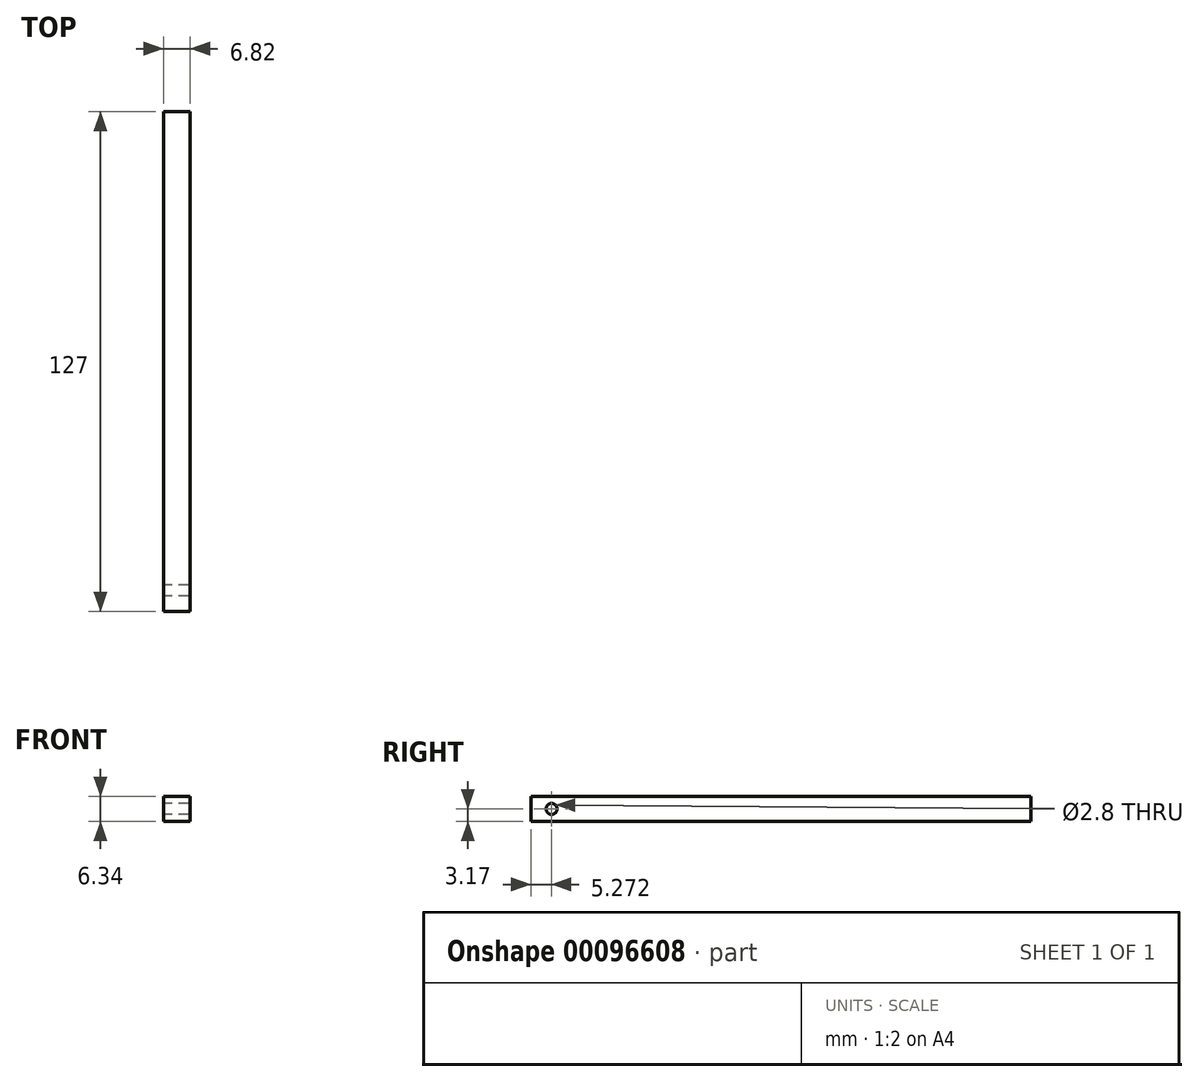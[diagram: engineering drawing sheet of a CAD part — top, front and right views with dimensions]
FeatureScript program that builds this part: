
annotation { "Feature Type Name" : "Feature", "Feature Type Description" : "" }
export const myFeature = defineFeature(function(context is Context, id is Id, definition is map)
    precondition{}
    {
        {
            var Q0;
            Q0=qCreatedBy(makeId("Front.planeOp"),FACE);
            var sketch = newSketch(context, id + "F0", { "sketchPlane" : qUnion([Q0])});
            skLineSegment(sketch, "E0.bottom", {"start": v(3.4, 3.18) * mm, "end": v(-3.4, 3.18) * mm});
            skLineSegment(sketch, "E0.top", {"start": v(3.4, -3.18) * mm, "end": v(-3.4, -3.18) * mm});
            skLineSegment(sketch, "E0.left", {"start": v(3.4, 3.17) * mm, "end": v(3.4, -3.17) * mm});
            skLineSegment(sketch, "E0.right", {"start": v(-3.4, 3.17) * mm, "end": v(-3.4, -3.17) * mm});
            skPoint(sketch, "E0.middle", {"position": v(0, 0) * mm});
            skSolve(sketch);
        }
        {
            var Q0;
            Q0 = qSketchRegion(id + "F0", true);
            extrude(context, id + "F1", {"entities" : qUnion([Q0]), "depth" : 127 * mm});
        }
        {
            var Q0;
            Q0=makeQuery(id+"F1.opExtrude","SWEPT_FACE",FACE,{"disambiguationData":[OSD([sQuery(id+"F0.wireOp",EDGE,"E0.right")])]});
            var sketch = newSketch(context, id + "F2", { "sketchPlane" : qUnion([Q0])});
            skLineSegment(sketch, "E1", {"start": v(127, 0) * mm, "end": v(121.73, 0) * mm});
            skPoint(sketch, "E1.endSnap0", {"position": v(127, 0) * mm});
            skLineSegment(sketch, "E2", {"start": v(121.73, 0) * mm, "end": v(127, 0) * mm});
            skCircle(sketch, "E3", {"center": v(121.73, 0) * mm, "radius": 1.4 * mm});
            skSolve(sketch);
        }
        {
            var Q0;
            Q0 = qSketchRegion(id + "F2", true);
            extrude(context, id + "F3", {"entities" : qUnion([Q0]), "operationType" : NewBodyOperationType.REMOVE, "endBound" : BoundingType.THROUGH_ALL, "oppositeDirection" : true, "depth" : 25.4 * mm});
        }
    });
